# Revit family: Seating-LAMMHULTS-GRADE_PLUS-5_Feet-Swivelbase
name_source: partatom
category: Furniture
revit_build: Autodesk Revit 2017 (Build: 20170816_0615(x64)
units: mm (PartAtom-declared; Revit-internal decimal feet)

## family parameters
Always vertical = Yes
Cut with Voids When Loaded = No
OmniClass Number = 23.40.20.00
OmniClass Title = General Furniture and Specialties
Room Calculation Point = No
Shared = No
Work Plane-Based = No

## types (3) — shared parameters
Assembly Code = E2020
Depth = 670 mm
Description = *Please enter mtrl description here for use in mto*
Height = 880 mm
Keynote = 46.B
Manufacturer = LAMMHULTS
Model = GRADE PLUS
URL = www.lammhults.se
Weight = 8.1 kg
Width = 700 mm

## per-type parameters (varying)
| type | Frame Material | Seat Material | Seat Pad Material |
| Crome-White | Metal - Chrome - Polished | Plastic - White | Colour - Khaki |
| Black-Black | Metal - Black - Matte | Plastic - Black | Colour - Khaki |
| Crome-Red | Metal - Chrome - Polished | Plastic - Red | Fabric - Red |

## geometry (parser evidence)
native form markers: Blend x8, Sweep x1
no freeform markers — native parametric forms only
